# Revit family: Shower-Handshower-KOHLER-Bancroft-K-22163
name_source: partatom
category: Plumbing Fixtures
revit_build: Autodesk Revit 2015 (Build: 20140606_1530(x64)
units: mm (PartAtom-declared; Revit-internal decimal feet)

## types (12) — shared parameters
ADA Compliant = Yes
Assembly Code = D2010700
CW Connection = No
Cold Water Inlet = Cold Water Inlet
Date Modified = 12/12/2018
Default Elevation = 72"
Drain Included = No
HW Connection = Yes
Height = 11 13/16"
Hot Water Inlet = Tempered Water Inlet
Length = 4 1/4"
Manufacturer = KOHLER Co.
MasterFormat 1995 = 15410
MasterFormat 2004 = 22.41.23
Material = Premium Metal Construction
Panel Thickness = 0"
Product Documentation Link = http://www.us.kohler.com
Product Name = Bancroft
Product Page URL = http://www.us.kohler.com
URL = https://www.us.kohler.com
Vent Connection = No
Waste Connection = No
Waste Water Outlet = Waste Water Outlet
Width = 5 3/16"

## per-type parameters (varying)
| type | Description | Finish | Flow Rate | Model | Type |
| 1.75 GPM,CP-Polished Chrome | 1.75 gpm multifunction handshower with Katalyst air-induction technology | Kohler-Metal-CP-Polished_Chrome | 2 GPM | K-22163-G-CP | 1 |
| 1.75 GPM,SN-Vibrant Polished Nickel | 1.75 gpm multifunction handshower with Katalyst air-induction technology | Kohler-Metal-SN-Vibrant_Polished_Nickel | 2 GPM | K-22163-G-SN | 2 |
| 1.75 GPM,PB-Vibrant Polished Brass | 1.75 gpm multifunction handshower with Katalyst air-induction technology | Kohler-Metal-PB-Vibrant_Polished_Brass | 2 GPM | K-22163-G-PB | 3 |
| 1.75 GPM,BN-Vibrant Brushed Nickel | 1.75 gpm multifunction handshower with Katalyst air-induction technology | Kohler-Metal-BN-Vibrant_Brushed_Nickel | 2 GPM | K-22163-G-BN | 4 |
| 1.75 GPM,BV-Vibrant Brushed Bronze | 1.75 gpm multifunction handshower with Katalyst air-induction technology | Kohler-Metal-BV-Brushed_Bronze | 2 GPM | K-22163-G-BV | 5 |
| 1.75 GPM,2BZ-Oil Rubbed Bronze | 1.75 gpm multifunction handshower with Katalyst air-induction technology | Kohler-Metal-2BZ-Oil_Rubbed_Bronze | 2 GPM | K-22163-G-2BZ | 6 |
| 2.5 GPM,CP-Polished Chrome | 2.5 gpm multifunction handshower with Katalyst air-induction technology | Kohler-Metal-CP-Polished_Chrome | 3 GPM | K-22163-CP | 7 |
| 2.5 GPM,SN-Vibrant Polished Nickel | 2.5 gpm multifunction handshower with Katalyst air-induction technology | Kohler-Metal-SN-Vibrant_Polished_Nickel | 3 GPM | K-22163-SN | 8 |
| 2.5 GPM,PB-Vibrant Polished Brass | 2.5 gpm multifunction handshower with Katalyst air-induction technology | Kohler-Metal-PB-Vibrant_Polished_Brass | 3 GPM | K-22163-PB | 9 |
| 2.5 GPM,BN-Vibrant Brushed Nickel | 2.5 gpm multifunction handshower with Katalyst air-induction technology | Kohler-Metal-BN-Vibrant_Brushed_Nickel | 3 GPM | K-22163-BN | 10 |
| 2.5 GPM,BV-Vibrant Brushed Bronze | 2.5 gpm multifunction handshower with Katalyst air-induction technology | Kohler-Metal-BV-Brushed_Bronze | 3 GPM | K-22163-BV | 11 |
| 2.5 GPM,2BZ-Oil Rubbed Bronze | 2.5 gpm multifunction handshower with Katalyst air-induction technology | Kohler-Metal-2BZ-Oil_Rubbed_Bronze | 3 GPM | K-22163-2BZ | 12 |

## geometry (parser evidence)
native form markers: Sweep x4
no freeform markers — native parametric forms only
